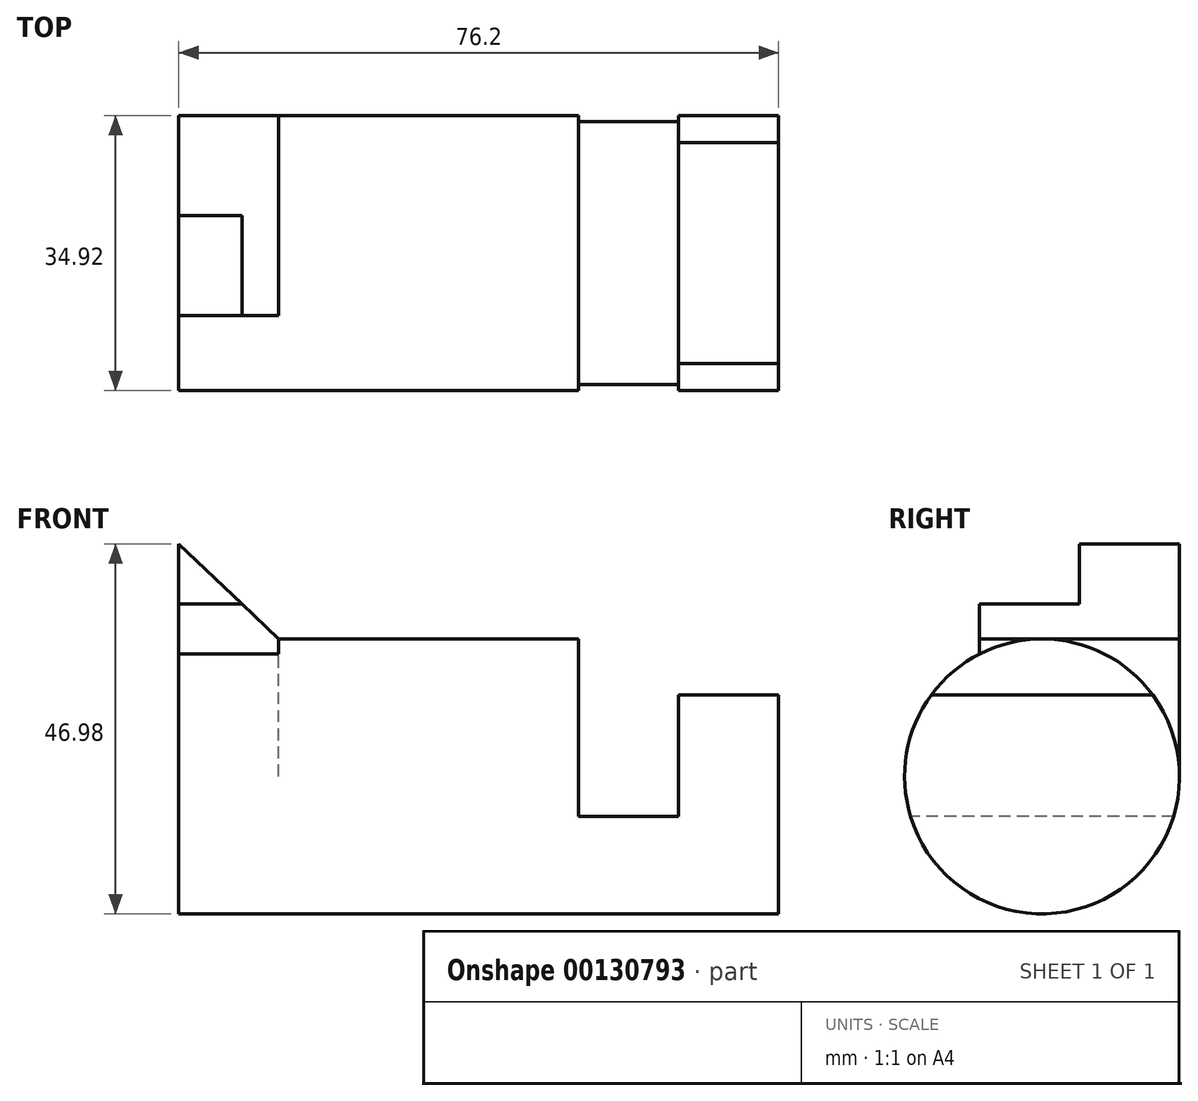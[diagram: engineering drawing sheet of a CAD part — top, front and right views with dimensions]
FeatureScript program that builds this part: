
annotation { "Feature Type Name" : "Feature", "Feature Type Description" : "" }
export const myFeature = defineFeature(function(context is Context, id is Id, definition is map)
    precondition{}
    {
        {
            var Q0;
            Q0=qCreatedBy(makeId("Right.planeOp"),FACE);
            var sketch = newSketch(context, id + "F0", { "sketchPlane" : qUnion([Q0])});
            skCircle(sketch, "E0", {"center": v(0, 0) * mm, "radius": 17.46 * mm});
            skSolve(sketch);
        }
        {
            var Q0;
            Q0 = qSketchRegion(id + "F0", true);
            extrude(context, id + "F1", {"entities" : qUnion([Q0]), "oppositeDirection" : true, "depth" : 76.2 * mm});
        }
        {
            var Q0;
            Q0=qCreatedBy(makeId("Front.planeOp"),FACE);
            var sketch = newSketch(context, id + "F2", { "sketchPlane" : qUnion([Q0])});
            skLineSegment(sketch, "E1", {"start": v(-12.7, 0) * mm, "end": v(-12.7, -5.08) * mm});
            skLineSegment(sketch, "E2", {"start": v(-12.7, -5.08) * mm, "end": v(-25.4, -5.08) * mm});
            skLineSegment(sketch, "E3", {"start": v(-25.4, -5.08) * mm, "end": v(-25.4, 33.02) * mm});
            skLineSegment(sketch, "E4", {"start": v(-25.4, 33.02) * mm, "end": v(0, 33.02) * mm});
            skLineSegment(sketch, "E5", {"start": v(0, 0) * mm, "end": v(0, -12.28) * mm, "construction": true});
            skLineSegment(sketch, "E6", {"start": v(0, -12.28) * mm, "end": v(-25.6, -12.28) * mm, "construction": true});
            skLineSegment(sketch, "E7", {"start": v(-25.6, -12.28) * mm, "end": v(-25.4, 33.02) * mm, "construction": true});
            skLineSegment(sketch, "E8", {"start": v(0, 33.02) * mm, "end": v(0, 10.37) * mm});
            skLineSegment(sketch, "E9", {"start": v(0, 10.37) * mm, "end": v(-12.7, 10.37) * mm});
            skLineSegment(sketch, "E10", {"start": v(-12.7, 10.37) * mm, "end": v(-12.7, 0) * mm});
            skSolve(sketch);
        }
        {
            var Q0;
            Q0 = qSketchRegion(id + "F2", true);
            extrude(context, id + "F3", {"entities" : qUnion([Q0]), "operationType" : NewBodyOperationType.REMOVE, "endBound" : BoundingType.SYMMETRIC, "oppositeDirection" : true, "depth" : 76.2 * mm});
        }
        {
            var Q0;
            Q0=makeQuery(id+"F3.boolean.opBoolean","COPY",FACE,{"derivedFrom":makeQuery(id+"F3.opExtrude","SWEPT_FACE",FACE,{"disambiguationData":[OSD([sQuery(id+"F2.wireOp",EDGE,"E3")])]})});
            var sketch = newSketch(context, id + "F4", { "sketchPlane" : qUnion([Q0])});
            skLineSegment(sketch, "E11", {"start": v(-7.94, 15.55) * mm, "end": v(-7.94, 21.9) * mm});
            skLineSegment(sketch, "E12", {"start": v(-7.94, 21.9) * mm, "end": v(4.76, 21.9) * mm});
            skLineSegment(sketch, "E13", {"start": v(4.76, 21.9) * mm, "end": v(4.76, 29.52) * mm});
            skLineSegment(sketch, "E14", {"start": v(17.46, 0) * mm, "end": v(17.46, 29.52) * mm});
            skLineSegment(sketch, "E15", {"start": v(17.46, 29.52) * mm, "end": v(4.76, 29.52) * mm});
            skSolve(sketch);
        }
        {
            var Q0;
            Q0 = qSketchRegion(id + "F4", true);
            var Q1;
            {var subQ1=sQuery(id+"F4.wireOp",EDGE,"E11");Q1=makeQuery(id+"F4.imprint","IMPRINT",FACE,{"disambiguationData":[TD([[makeQuery(id+"F4.imprint","IMPRINT",EDGE,{"derivedFrom":subQ1}),-1.0]])]});}
            extrude(context, id + "F5", {"entities" : qUnion([Q0, Q1]), "operationType" : NewBodyOperationType.ADD, "oppositeDirection" : true, "depth" : 50.8 * mm, "hasSecondDirection" : true, "secondDirectionOppositeDirection" : true, "secondDirectionDepth" : 38.1 * mm});
        }
        {
            var Q0;
            Q0=qCreatedBy(makeId("Front.planeOp"),FACE);
            var sketch = newSketch(context, id + "F6", { "sketchPlane" : qUnion([Q0])});
            skLineSegment(sketch, "E16", {"start": v(-76.2, 29.52) * mm, "end": v(-63.5, 29.52) * mm});
            skLineSegment(sketch, "E17", {"start": v(-76.2, 29.52) * mm, "end": v(-63.5, 17.5) * mm});
            skLineSegment(sketch, "E18", {"start": v(-63.5, 17.5) * mm, "end": v(-63.5, 29.52) * mm});
            skSolve(sketch);
        }
        {
            var Q0;
            Q0 = qSketchRegion(id + "F6", true);
            extrude(context, id + "F7", {"entities" : qUnion([Q0]), "operationType" : NewBodyOperationType.REMOVE, "endBound" : BoundingType.SYMMETRIC, "oppositeDirection" : true, "depth" : 50.8 * mm});
        }
    });
